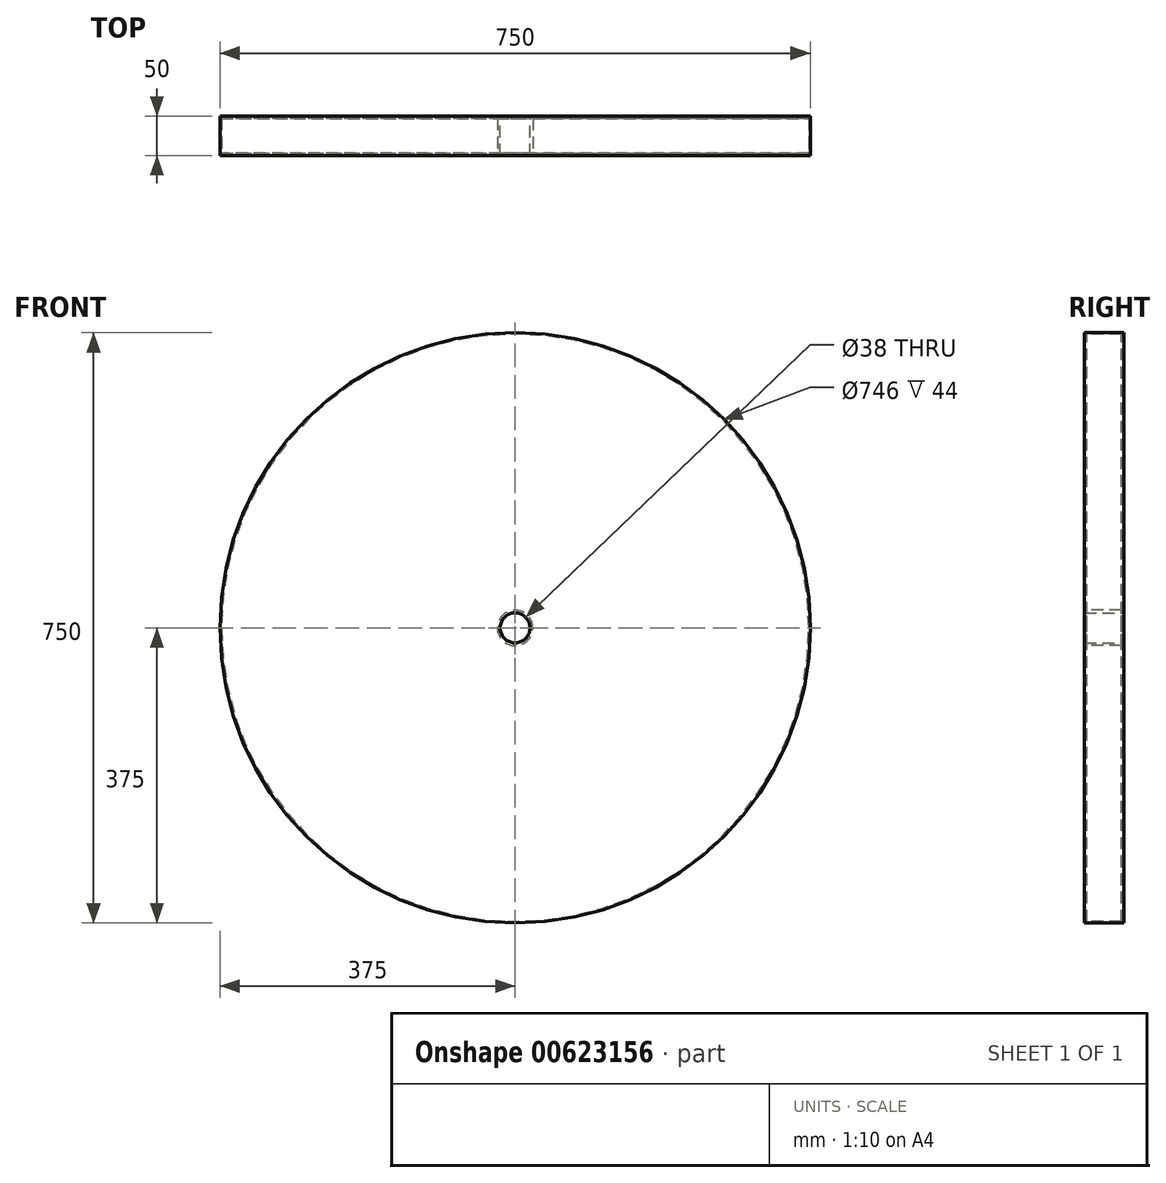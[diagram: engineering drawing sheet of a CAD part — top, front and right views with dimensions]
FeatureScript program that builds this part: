
annotation { "Feature Type Name" : "Feature", "Feature Type Description" : "" }
export const myFeature = defineFeature(function(context is Context, id is Id, definition is map)
    precondition{}
    {
        {
            var Q0;
            Q0=qCreatedBy(makeId("Front.planeOp"),FACE);
            var sketch = newSketch(context, id + "F0", { "sketchPlane" : qUnion([Q0])});
            skCircle(sketch, "E0", {"center": v(0, 0) * mm, "radius": 375 * mm});
            skCircle(sketch, "E1", {"center": v(0, 0) * mm, "radius": 19 * mm});
            skSolve(sketch);
        }
        {
            var Q0;
            Q0=qSketchRegion(id+"F0",true);
            extrude(context, id + "F1", {"entities" : qUnion([Q0]), "depth" : 50 * mm, "offsetDistance" : 25 * mm});
        }
        {
            var Q0;
            Q0=makeQuery(id+"F1.opExtrude","CAP_FACE",FACE,{"disambiguationData":[OSD([sQuery(id+"F0.wireOp",EDGE,"E0"),sQuery(id+"F0.wireOp",EDGE,"E1")])],"isStart":false});
            cPlane(context, id + "F2", {"entities" : qUnion([Q0]), "cplaneType" : CPlaneType.OFFSET, "offset" : 3 * mm, "oppositeDirection" : true, "width" : 150 * mm, "height" : 150 * mm});
        }
        {
            var Q0;
            Q0=qCreatedBy(id+"F2.planeOp",FACE);
            var sketch = newSketch(context, id + "F3", { "sketchPlane" : qUnion([Q0])});
            skCircle(sketch, "E2.0", {"center": v(0, 0) * mm, "radius": 19 * mm, "construction": true});
            skCircle(sketch, "E3", {"center": v(0, 0) * mm, "radius": 373 * mm});
            skCircle(sketch, "E4", {"center": v(0, 0) * mm, "radius": 22.5 * mm});
            skSolve(sketch);
        }
        {
            var Q0;
            Q0=qSketchRegion(id+"F3",true);
            extrude(context, id + "F4", {"entities" : qUnion([Q0]), "operationType" : NewBodyOperationType.REMOVE, "oppositeDirection" : true, "depth" : 44 * mm, "offsetDistance" : 25 * mm});
        }
    });
